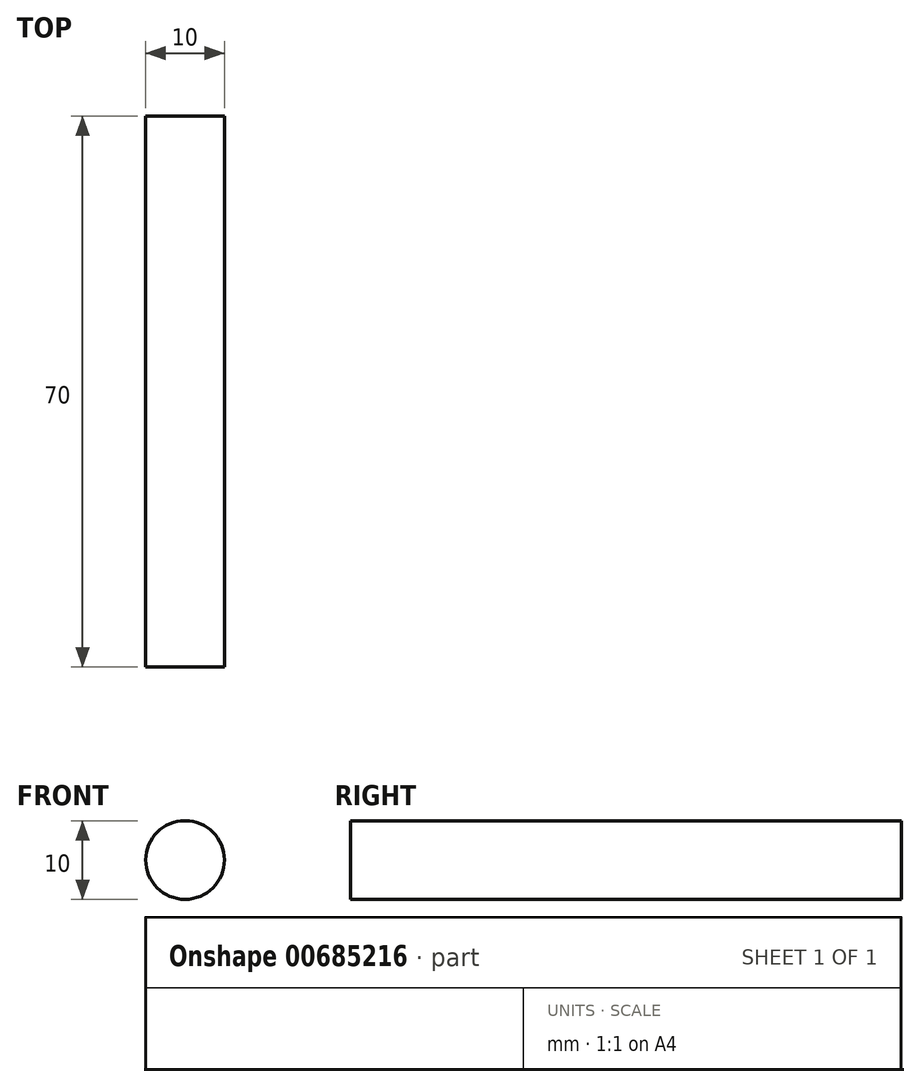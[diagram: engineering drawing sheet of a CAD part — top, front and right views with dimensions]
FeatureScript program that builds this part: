
annotation { "Feature Type Name" : "Feature", "Feature Type Description" : "" }
export const myFeature = defineFeature(function(context is Context, id is Id, definition is map)
    precondition{}
    {
        {
            var Q0;
            Q0=qCreatedBy(makeId("Front.planeOp"),FACE);
            var sketch = newSketch(context, id + "F0", { "sketchPlane" : qUnion([Q0])});
            skCircle(sketch, "E0", {"center": v(0, 0) * mm, "radius": 5 * mm});
            skSolve(sketch);
        }
        {
            var Q0;
            Q0=makeQuery(id+"F0.imprint","IMPRINT",FACE,{"disambiguationData":[TD([[makeQuery(id+"F0.imprint","IMPRINT",EDGE,{"derivedFrom":sQuery(id+"F0.wireOp",EDGE,"E0")}),1.0]])]});
            extrude(context, id + "F1", {"entities" : qUnion([Q0]), "depth" : 70 * mm, "offsetDistance" : 25 * mm});
        }
    });
